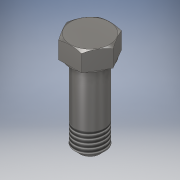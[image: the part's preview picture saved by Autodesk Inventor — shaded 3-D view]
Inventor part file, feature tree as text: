
AUTODESK INVENTOR PART (.ipt)
format: ipt  version: 2018 (Build 220112000, 112)  size: 153,088 bytes
history: native  units: in
note: dims shown in document units (in); Inventor stores cm internally (conversion verified against a paired STEP export)
features: sketch x3, revolve x2, extrude x2, chamfer x1, thread x1, projected_geometry x1
ambient origin geometry x8: Origin, YZ Plane, XZ Plane, XY Plane, X Axis, Y Axis, Z Axis, Center Point
bodies: Solid1 (feature_tree)
feature tree (10):
  revolve  "Revolution1"  [1 undecoded]
  chamfer  "Chamfer1"  Distance=0.125in Angle=45.0deg
  extrude  "Extrusion1"  Depth=0.5in TaperAngle=0.0deg
  extrude  "Extrusion2"  Depth=0.47in TaperAngle=0.0deg
  revolve  "Revolution2"  Angle=30.0deg
  thread  "Thread2"  [1 undecoded]
  sketch  "Sketch1"  dims[d0=0.75in d1=2.0in]
  sketch  "Sketch2"  dims[d2=90.0deg d3=0.125in d4=0.125in d5=45.0deg]
  sketch  "Sketch3"  dims[d6=1.0in d7=0.5in d8=0.0in d9=0.47in d10=0.0in d11=30.0deg d12=90.0deg d17=0.05in d19=0.5in d20=0.0in]
  projected_geometry  "Projected Loop1"
note: 2 required parameter values undecoded (feature->parameter linkage not recoverable at this tier; creation-order binding heuristic only, values carry confidence <= 0.55)